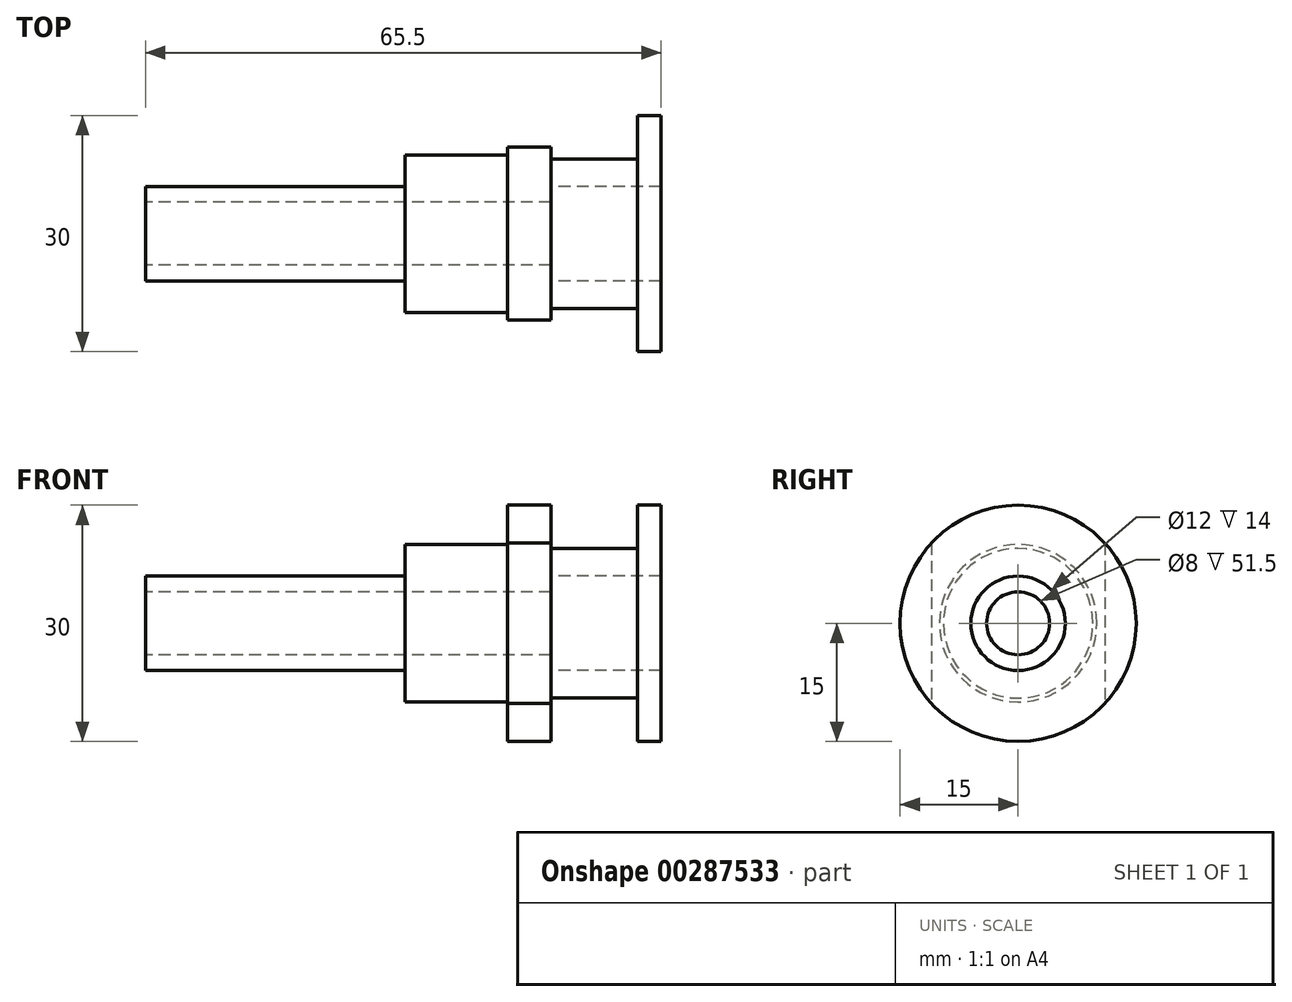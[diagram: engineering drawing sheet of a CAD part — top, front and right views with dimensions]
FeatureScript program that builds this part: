
annotation { "Feature Type Name" : "Feature", "Feature Type Description" : "" }
export const myFeature = defineFeature(function(context is Context, id is Id, definition is map)
    precondition{}
    {
        {
            var Q0;
            Q0=qCreatedBy(makeId("Front.planeOp"),FACE);
            var sketch = newSketch(context, id + "F0", { "sketchPlane" : qUnion([Q0])});
            skLineSegment(sketch, "E0", {"start": v(0, 0) * mm, "end": v(33, 0) * mm});
            skLineSegment(sketch, "E1", {"start": v(0, 0) * mm, "end": v(0, 6) * mm});
            skLineSegment(sketch, "E2", {"start": v(0, 6) * mm, "end": v(33, 6) * mm});
            skLineSegment(sketch, "E3", {"start": v(33, 6) * mm, "end": v(33, 0) * mm});
            skLineSegment(sketch, "E4", {"start": v(33, 0) * mm, "end": v(46, 0) * mm});
            skLineSegment(sketch, "E5", {"start": v(46, 0) * mm, "end": v(46, 10) * mm});
            skLineSegment(sketch, "E6", {"start": v(46, 10) * mm, "end": v(33, 10) * mm});
            skLineSegment(sketch, "E7", {"start": v(33, 10) * mm, "end": v(33, 6) * mm});
            skLineSegment(sketch, "E8", {"start": v(46, 0) * mm, "end": v(51.5, 0) * mm});
            skLineSegment(sketch, "E9", {"start": v(51.5, 0) * mm, "end": v(51.5, 15) * mm});
            skLineSegment(sketch, "E10", {"start": v(51.5, 15) * mm, "end": v(46, 15) * mm});
            skLineSegment(sketch, "E11", {"start": v(46, 15) * mm, "end": v(46, 10) * mm});
            skLineSegment(sketch, "E12", {"start": v(51.5, 0) * mm, "end": v(62.5, 0) * mm});
            skLineSegment(sketch, "E13", {"start": v(62.5, 0) * mm, "end": v(62.5, 9.5) * mm});
            skLineSegment(sketch, "E14", {"start": v(62.5, 9.5) * mm, "end": v(51.5, 9.5) * mm});
            skLineSegment(sketch, "E15", {"start": v(62.5, 0) * mm, "end": v(65.5, 0) * mm});
            skLineSegment(sketch, "E16", {"start": v(65.5, 0) * mm, "end": v(65.5, 15) * mm});
            skLineSegment(sketch, "E17", {"start": v(65.5, 15) * mm, "end": v(62.5, 15) * mm});
            skLineSegment(sketch, "E18", {"start": v(62.5, 15) * mm, "end": v(62.5, 9.5) * mm});
            skPoint(sketch, "E19", {"position": v(65.5, 6) * mm});
            skLineSegment(sketch, "E20", {"start": v(65.5, 6) * mm, "end": v(51.5, 6) * mm});
            skPoint(sketch, "E21", {"position": v(0, 4) * mm});
            skLineSegment(sketch, "E22", {"start": v(0, 4) * mm, "end": v(51.5, 4) * mm});
            skSolve(sketch);
        }
        {
            var Q0;
            {var subQ1=sQuery(id+"F0.wireOp",EDGE,"E17");Q0=makeQuery(id+"F0.imprint","IMPRINT",FACE,{"disambiguationData":[TD([[makeQuery(id+"F0.imprint","IMPRINT",EDGE,{"derivedFrom":subQ1}),1.0]])]});}
            var Q1;
            {var subQ0=sQuery(id+"F0.wireOp",EDGE,"E14");Q1=makeQuery(id+"F0.imprint","IMPRINT",FACE,{"disambiguationData":[TD([[makeQuery(id+"F0.imprint","IMPRINT",EDGE,{"derivedFrom":subQ0}),1.0]])]});}
            var Q2;
            {var subQ0=sQuery(id+"F0.wireOp",EDGE,"E2");Q2=makeQuery(id+"F0.imprint","IMPRINT",FACE,{"disambiguationData":[TD([[makeQuery(id+"F0.imprint","IMPRINT",EDGE,{"derivedFrom":subQ0}),-1.0]])]});}
            var Q3;
            {var subQ1=sQuery(id+"F0.wireOp",EDGE,"E6");Q3=makeQuery(id+"F0.imprint","IMPRINT",FACE,{"disambiguationData":[TD([[makeQuery(id+"F0.imprint","IMPRINT",EDGE,{"derivedFrom":subQ1}),1.0]])]});}
            var Q4;
            {var subQ0=sQuery(id+"F0.wireOp",EDGE,"E10");Q4=makeQuery(id+"F0.imprint","IMPRINT",FACE,{"disambiguationData":[TD([[makeQuery(id+"F0.imprint","IMPRINT",EDGE,{"derivedFrom":subQ0}),1.0]])]});}
            var Q5;
            Q5=sQuery(id+"F0.wireOp",EDGE,"E0");
            revolve(context, id + "F1", {"entities" : qUnion([Q0, Q1, Q2, Q3, Q4]), "axis" : qUnion([Q5]), "revolveType" : RevolveType.FULL});
        }
        {
            var Q0;
            Q0=makeQuery(id+"F1.opRevolve","SWEPT_FACE",FACE,{"disambiguationData":[OSD([sQuery(id+"F0.wireOp",EDGE,"E11")])]});
            var sketch = newSketch(context, id + "F2", { "sketchPlane" : qUnion([Q0])});
            skCircle(sketch, "E23.0", {"center": v(0, 0) * mm, "radius": 10 * mm});
            skLineSegment(sketch, "E24", {"start": v(0, 0) * mm, "end": v(11, 0) * mm});
            skLineSegment(sketch, "E25", {"start": v(0, 0) * mm, "end": v(-11, 0) * mm});
            skCircle(sketch, "E26.0", {"center": v(0, 0) * mm, "radius": 15 * mm});
            skLineSegment(sketch, "E27", {"start": v(-11, 10.2) * mm, "end": v(-11, -10.2) * mm});
            skLineSegment(sketch, "E28", {"start": v(11, 10.2) * mm, "end": v(11, -10.2) * mm});
            skSolve(sketch);
        }
        {
            var Q0;
            {var subQ0=sQuery(id+"F2.wireOp",EDGE,"E27");var subQ1=sQuery(id+"F2.wireOp",EDGE,"E26.0");var subQ2=makeQuery(id+"F2.imprint","INTERSECT",VERTEX,{"disambiguationData":[OD(0.0)],"derivedFrom":[subQ1,subQ0]});Q0=makeQuery(id+"F2.imprint","IMPRINT",FACE,{"disambiguationData":[TD([[makeQuery(id+"F2.imprint","IMPRINT",EDGE,{"disambiguationData":[TD([[subQ2,-1.0]])],"derivedFrom":subQ1}),1.0]])]});}
            var Q1;
            {var subQ0=sQuery(id+"F2.wireOp",EDGE,"E28");var subQ1=sQuery(id+"F2.wireOp",EDGE,"E26.0");var subQ2=makeQuery(id+"F2.imprint","INTERSECT",VERTEX,{"disambiguationData":[OD(0.0)],"derivedFrom":[subQ1,subQ0]});Q1=makeQuery(id+"F2.imprint","IMPRINT",FACE,{"disambiguationData":[TD([[makeQuery(id+"F2.imprint","IMPRINT",EDGE,{"disambiguationData":[TD([[subQ2,1.0]])],"derivedFrom":subQ1}),1.0]])]});}
            extrude(context, id + "F3", {"entities" : qUnion([Q0, Q1]), "operationType" : NewBodyOperationType.REMOVE, "oppositeDirection" : true, "depth" : 5.5 * mm});
        }
    });
